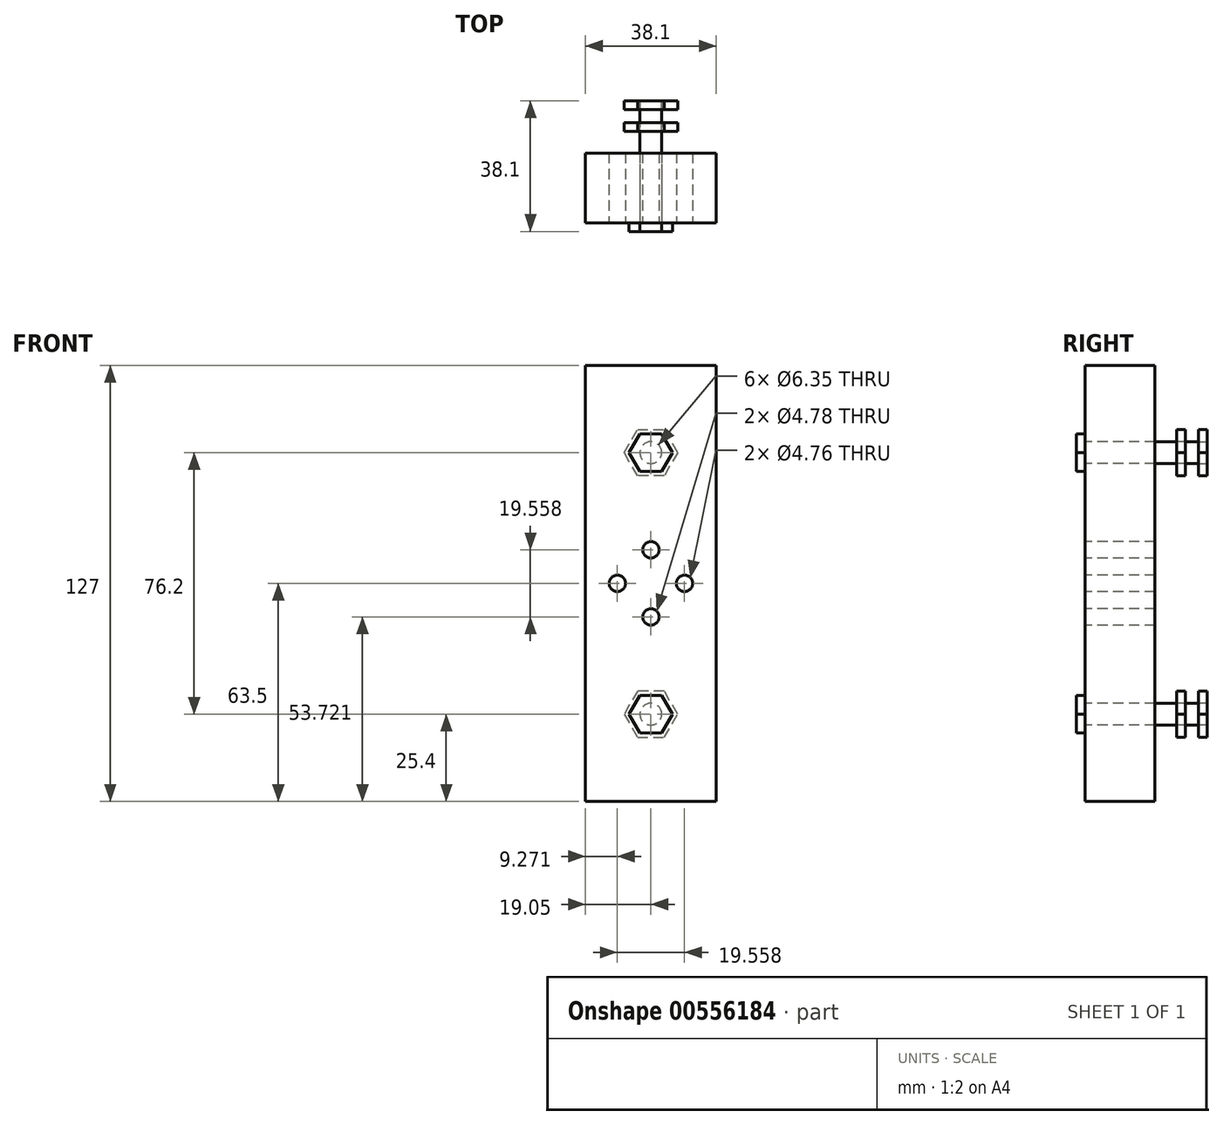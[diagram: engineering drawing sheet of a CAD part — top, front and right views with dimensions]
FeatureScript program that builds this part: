
annotation { "Feature Type Name" : "Feature", "Feature Type Description" : "" }
export const myFeature = defineFeature(function(context is Context, id is Id, definition is map)
    precondition{}
    {
        {
            var Q0;
            Q0=qCreatedBy(makeId("Front.planeOp"),FACE);
            var sketch = newSketch(context, id + "F0", { "sketchPlane" : qUnion([Q0])});
            skLineSegment(sketch, "E0.0", {"start": v(6.35, 0) * mm, "end": v(3.18, -5.5) * mm});
            skLineSegment(sketch, "E0.1", {"start": v(3.18, -5.5) * mm, "end": v(-3.17, -5.5) * mm});
            skLineSegment(sketch, "E0.2", {"start": v(-3.17, -5.5) * mm, "end": v(-6.35, 0) * mm});
            skLineSegment(sketch, "E0.3", {"start": v(-6.35, 0) * mm, "end": v(-3.18, 5.5) * mm});
            skLineSegment(sketch, "E0.4", {"start": v(-3.18, 5.5) * mm, "end": v(3.17, 5.5) * mm});
            skLineSegment(sketch, "E0.5", {"start": v(3.17, 5.5) * mm, "end": v(6.35, 0) * mm});
            skSolve(sketch);
        }
        {
            var Q0;
            Q0 = qSketchRegion(id + "F0", true);
            extrude(context, id + "F1", {"entities" : qUnion([Q0]), "depth" : 2.54 * mm, "offsetDistance" : 25.4 * mm});
        }
        {
            var Q0;
            Q0=makeQuery(id+"F1.opExtrude","CAP_FACE",FACE,{"disambiguationData":[OSD([sQuery(id+"F0.wireOp",EDGE,"E0.0"),sQuery(id+"F0.wireOp",EDGE,"E0.1"),sQuery(id+"F0.wireOp",EDGE,"E0.2"),sQuery(id+"F0.wireOp",EDGE,"E0.3"),sQuery(id+"F0.wireOp",EDGE,"E0.4"),sQuery(id+"F0.wireOp",EDGE,"E0.5")])],"isStart":true});
            var sketch = newSketch(context, id + "F2", { "sketchPlane" : qUnion([Q0])});
            skCircle(sketch, "E1", {"center": v(0, 0) * mm, "radius": 3.18 * mm});
            skSolve(sketch);
        }
        {
            var Q0;
            Q0=makeQuery(id+"F2.imprint","IMPRINT",FACE,{"disambiguationData":[TD([[makeQuery(id+"F2.imprint","IMPRINT",EDGE,{"derivedFrom":sQuery(id+"F2.wireOp",EDGE,"E1")}),1.0]])]});
            extrude(context, id + "F3", {"entities" : qUnion([Q0]), "operationType" : NewBodyOperationType.ADD, "depth" : 35.56 * mm, "offsetDistance" : 25.4 * mm});
        }
        {
            var Q0;
            Q0=qCreatedBy(makeId("Front.planeOp"),FACE);
            var sketch = newSketch(context, id + "F4", { "sketchPlane" : qUnion([Q0])});
            skLineSegment(sketch, "E2", {"start": v(0, 101.6) * mm, "end": v(-19.05, 101.6) * mm});
            skLineSegment(sketch, "E3", {"start": v(0, 101.6) * mm, "end": v(19.05, 101.6) * mm});
            skLineSegment(sketch, "E4", {"start": v(19.05, 101.6) * mm, "end": v(19.05, -25.4) * mm});
            skLineSegment(sketch, "E5", {"start": v(19.05, -25.4) * mm, "end": v(-19.05, -25.4) * mm});
            skLineSegment(sketch, "E6", {"start": v(-19.05, -25.4) * mm, "end": v(-19.05, 101.6) * mm});
            skCircle(sketch, "E7", {"center": v(0, 76.2) * mm, "radius": 3.18 * mm});
            skLineSegment(sketch, "E8", {"start": v(-19.05, 38.1) * mm, "end": v(19.05, 38.1) * mm});
            skCircle(sketch, "E9", {"center": v(-9.78, 38.1) * mm, "radius": 2.38 * mm});
            skCircle(sketch, "E10", {"center": v(9.78, 38.1) * mm, "radius": 2.38 * mm});
            skCircle(sketch, "E11", {"center": v(0, 0) * mm, "radius": 3.18 * mm});
            skLineSegment(sketch, "E12", {"start": v(0, 38.1) * mm, "end": v(0, 28.32) * mm});
            skCircle(sketch, "E13", {"center": v(0, 28.32) * mm, "radius": 2.39 * mm});
            skLineSegment(sketch, "E14", {"start": v(0, 38.1) * mm, "end": v(0, 47.88) * mm});
            skCircle(sketch, "E15", {"center": v(0, 47.88) * mm, "radius": 2.39 * mm});
            skSolve(sketch);
        }
        {
            var Q0;
            Q0 = qSketchRegion(id + "F4", true);
            extrude(context, id + "F5", {"entities" : qUnion([Q0]), "oppositeDirection" : true, "depth" : 20.32 * mm, "offsetDistance" : 25.4 * mm});
        }
        {
            var Q0;
            Q0=makeQuery(id+"F5.opExtrude","SWEPT_FACE",FACE,{"disambiguationData":[OSD([sQuery(id+"F4.wireOp",EDGE,"E5")])]});
            cPlane(context, id + "F6", {"entities" : qUnion([Q0]), "cplaneType" : CPlaneType.OFFSET, "offset" : 63.5 * mm, "oppositeDirection" : true, "width" : 152.4 * mm, "height" : 152.4 * mm});
        }
        {
            var Q0;
            Q0=makeQuery(id+"F1.opExtrude","SWEPT_BODY",BODY,{"disambiguationData":[OSD([sQuery(id+"F0.wireOp",EDGE,"E0.0"),sQuery(id+"F0.wireOp",EDGE,"E0.1"),sQuery(id+"F0.wireOp",EDGE,"E0.2"),sQuery(id+"F0.wireOp",EDGE,"E0.3"),sQuery(id+"F0.wireOp",EDGE,"E0.4"),sQuery(id+"F0.wireOp",EDGE,"E0.5")])]});
            var Q1;
            Q1=qCreatedBy(id+"F6.planeOp",FACE);
            mirror(context, id + "F7", {"entities" : qUnion([Q0]), "mirrorPlane" : qUnion([Q1])});
        }
        {
            var Q0;
            Q0=makeQuery(id+"F3.opExtrude","CAP_FACE",FACE,{"disambiguationData":[OSD([sQuery(id+"F2.wireOp",EDGE,"E1")])],"isStart":false});
            var sketch = newSketch(context, id + "F8", { "sketchPlane" : qUnion([Q0])});
            skCircle(sketch, "E16.cCircle", {"center": v(0, 0) * mm, "radius": 6.74 * mm, "construction": true});
            skLineSegment(sketch, "E16.0", {"start": v(-3.9, 6.74) * mm, "end": v(3.9, 6.74) * mm});
            skLineSegment(sketch, "E16.1", {"start": v(3.9, 6.74) * mm, "end": v(7.79, 0) * mm});
            skLineSegment(sketch, "E16.2", {"start": v(7.79, 0) * mm, "end": v(3.9, -6.74) * mm});
            skLineSegment(sketch, "E16.3", {"start": v(3.9, -6.74) * mm, "end": v(-3.9, -6.74) * mm});
            skLineSegment(sketch, "E16.4", {"start": v(-3.9, -6.74) * mm, "end": v(-7.79, 0) * mm});
            skLineSegment(sketch, "E16.5", {"start": v(-7.79, 0) * mm, "end": v(-3.9, 6.74) * mm});
            skPoint(sketch, "E16.0.midPoint", {"position": v(0, 6.74) * mm});
            skPoint(sketch, "E17", {"position": v(0, 3.18) * mm});
            skCircle(sketch, "E18", {"center": v(0, 0) * mm, "radius": 3.18 * mm});
            skSolve(sketch);
        }
        {
            var Q0;
            Q0 = qSketchRegion(id + "F8", true);
            extrude(context, id + "F9", {"entities" : qUnion([Q0]), "oppositeDirection" : true, "depth" : 2.54 * mm, "offsetDistance" : 25.4 * mm});
        }
        {
            var Q0;
            Q0=makeQuery(id+"F9.opExtrude","SWEPT_BODY",BODY,{"disambiguationData":[OSD([sQuery(id+"F8.wireOp",EDGE,"E16.0"),sQuery(id+"F8.wireOp",EDGE,"E16.1"),sQuery(id+"F8.wireOp",EDGE,"E16.2"),sQuery(id+"F8.wireOp",EDGE,"E16.3"),sQuery(id+"F8.wireOp",EDGE,"E16.4"),sQuery(id+"F8.wireOp",EDGE,"E16.5"),sQuery(id+"F8.wireOp",EDGE,"E18")])]});
            var Q1;
            Q1=makeQuery(id+"F3.opExtrude","CAP_FACE",FACE,{"disambiguationData":[OSD([sQuery(id+"F2.wireOp",EDGE,"E1")])],"isStart":false});
            transform(context, id + "F10", {"entities" : qUnion([Q0]), "transformType" : TransformType.TRANSLATION_DISTANCE, "transformDirection" : qUnion([Q1]), "distance" : 6.35 * mm, "oppositeDirection" : true, "makeCopy" : true});
        }
        {
            var Q0;
            Q0=makeQuery(id+"F10.opPattern","COPY",BODY,{"derivedFrom":makeQuery(id+"F9.opExtrude","SWEPT_BODY",BODY,{"disambiguationData":[OSD([sQuery(id+"F8.wireOp",EDGE,"E16.0"),sQuery(id+"F8.wireOp",EDGE,"E16.1"),sQuery(id+"F8.wireOp",EDGE,"E16.2"),sQuery(id+"F8.wireOp",EDGE,"E16.3"),sQuery(id+"F8.wireOp",EDGE,"E16.4"),sQuery(id+"F8.wireOp",EDGE,"E16.5"),sQuery(id+"F8.wireOp",EDGE,"E18")])]}),"instanceName":"1"});
            var Q1;
            Q1=makeQuery(id+"F9.opExtrude","SWEPT_BODY",BODY,{"disambiguationData":[OSD([sQuery(id+"F8.wireOp",EDGE,"E16.0"),sQuery(id+"F8.wireOp",EDGE,"E16.1"),sQuery(id+"F8.wireOp",EDGE,"E16.2"),sQuery(id+"F8.wireOp",EDGE,"E16.3"),sQuery(id+"F8.wireOp",EDGE,"E16.4"),sQuery(id+"F8.wireOp",EDGE,"E16.5"),sQuery(id+"F8.wireOp",EDGE,"E18")])]});
            var Q2;
            Q2=qCreatedBy(id+"F6.planeOp",FACE);
            mirror(context, id + "F11", {"entities" : qUnion([Q0, Q1]), "mirrorPlane" : qUnion([Q2])});
        }
    });
